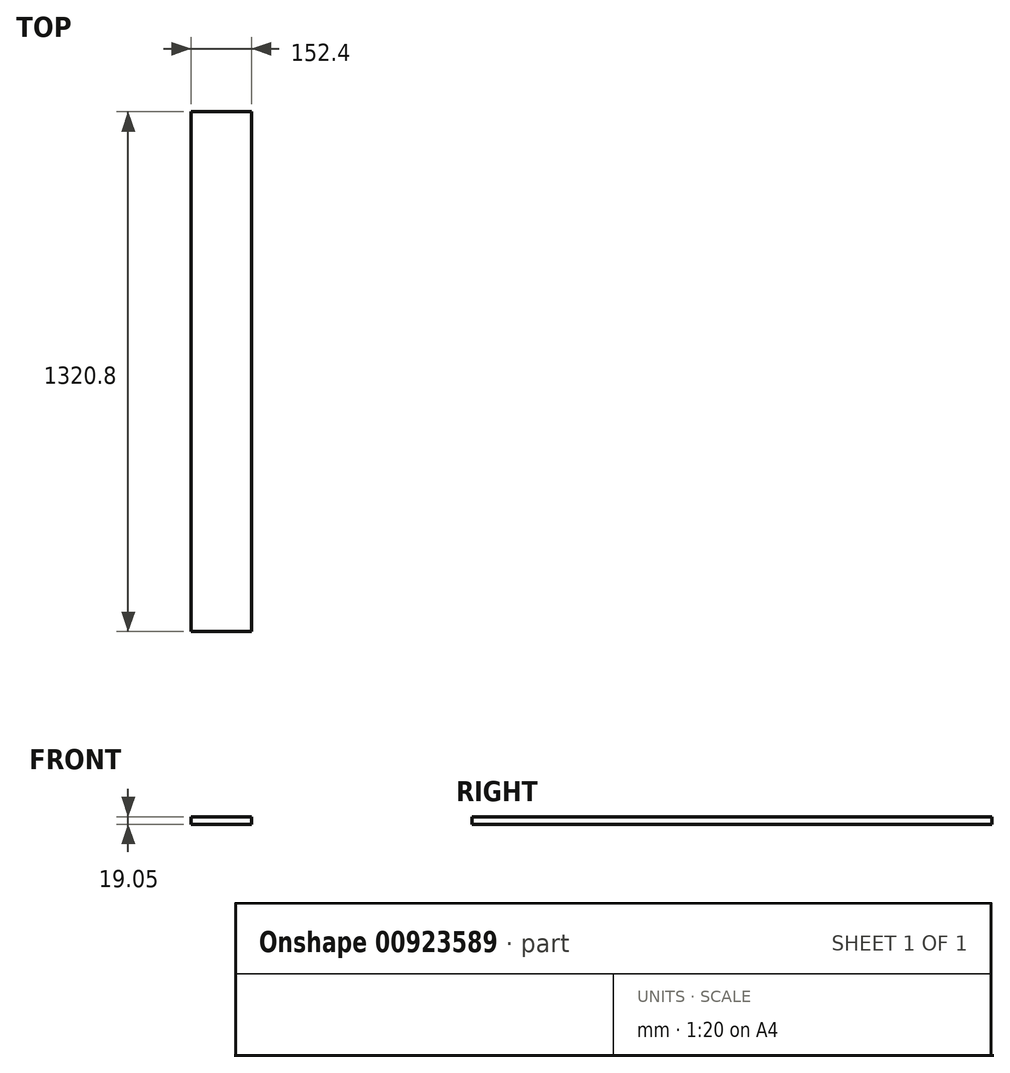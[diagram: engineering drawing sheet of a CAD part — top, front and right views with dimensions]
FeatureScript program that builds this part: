
annotation { "Feature Type Name" : "Feature", "Feature Type Description" : "" }
export const myFeature = defineFeature(function(context is Context, id is Id, definition is map)
    precondition{}
    {
        {
            var Q0;
            Q0=qCreatedBy(makeId("Top.planeOp"),FACE);
            var sketch = newSketch(context, id + "F0", { "sketchPlane" : qUnion([Q0])});
            skLineSegment(sketch, "E0.bottom", {"start": v(0, 0) * mm, "end": v(152.4, 0) * mm});
            skLineSegment(sketch, "E0.top", {"start": v(0, 1320.8) * mm, "end": v(152.4, 1320.8) * mm});
            skLineSegment(sketch, "E0.left", {"start": v(0, 0) * mm, "end": v(0, 1320.8) * mm});
            skLineSegment(sketch, "E0.right", {"start": v(152.4, 0) * mm, "end": v(152.4, 1320.8) * mm});
            skSolve(sketch);
        }
        {
            var Q0;
            Q0 = qSketchRegion(id + "F0", true);
            extrude(context, id + "F1", {"entities" : qUnion([Q0]), "depth" : 19.05 * mm, "offsetDistance" : 25.4 * mm});
        }
    });
